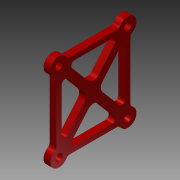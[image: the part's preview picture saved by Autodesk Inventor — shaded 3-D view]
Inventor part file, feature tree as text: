
AUTODESK INVENTOR PART (.ipt)
format: ipt  version: 2015 (Build 190159000, 159)  size: 158,720 bytes
history: native  units: mm
features: other x4, sketch x1
ambient origin geometry x8: Origin, YZ Plane, XZ Plane, XY Plane, X Axis, Y Axis, Z Axis, Center Point
bodies: Body1 (feature_tree)
feature tree (5):
  other  "Alignment_narrow.ipt"
  other  "Sólido1::Alignment_narrow.ipt"
  other  "OperaciónIdentificador1"
  sketch  "Boceto1"  dims[d0=10.0mm]
  other  "Sólido1"
